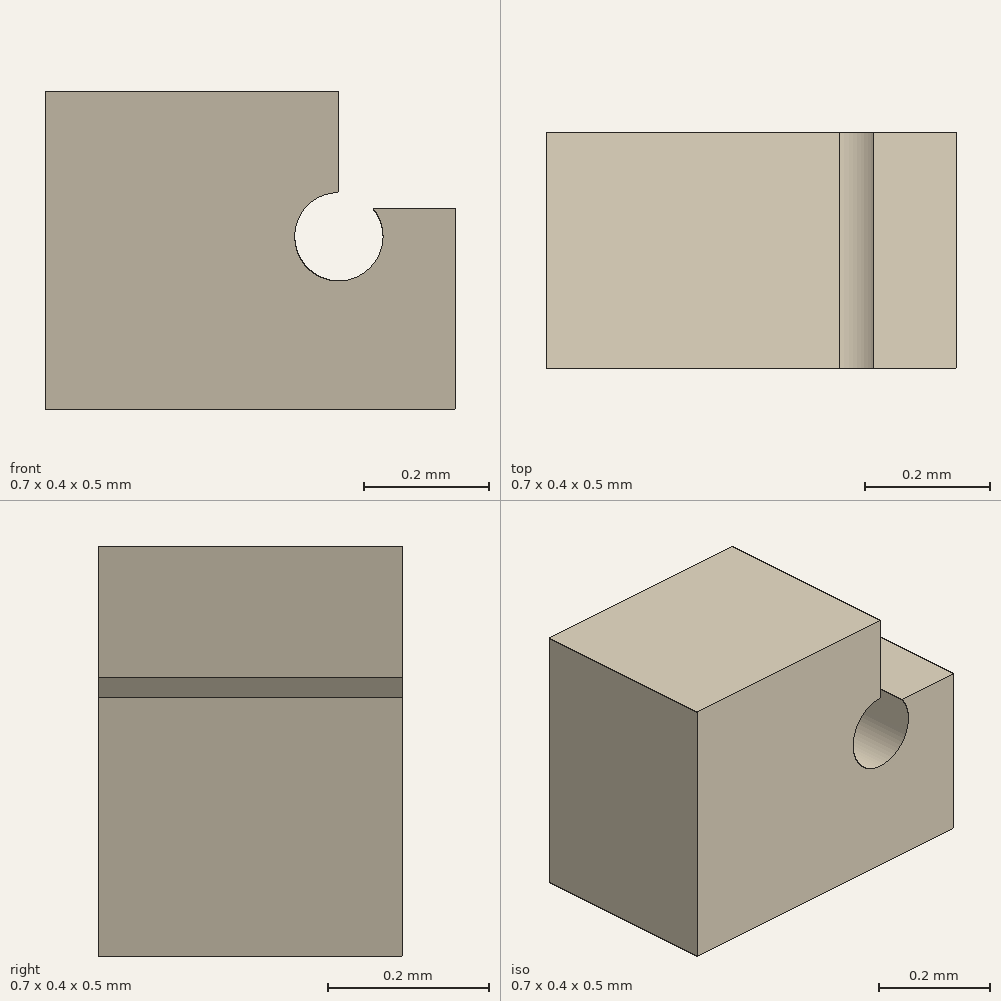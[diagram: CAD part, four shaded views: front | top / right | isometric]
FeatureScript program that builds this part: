
annotation { "Feature Type Name" : "Feature", "Feature Type Description" : "" }
export const myFeature = defineFeature(function(context is Context, id is Id, definition is map)
    precondition{}
    {
        {
            var Q0;
            Q0=qCreatedBy(makeId("Front.planeOp"),FACE);
            var sketch = newSketch(context, id + "F0", { "sketchPlane" : qUnion([Q0])});
            skLineSegment(sketch, "E0", {"start": v(0, 0) * mm, "end": v(0.94, 0) * mm});
            skLineSegment(sketch, "E1", {"start": v(0, 0) * mm, "end": v(0, 0.44) * mm});
            skLineSegment(sketch, "E2", {"start": v(0, 0.44) * mm, "end": v(0.94, 0.44) * mm});
            skLineSegment(sketch, "E3", {"start": v(0.94, 0.44) * mm, "end": v(0.94, 0) * mm});
            skLineSegment(sketch, "E4", {"start": v(0, 0.22) * mm, "end": v(0.94, 0.22) * mm});
            skLineSegment(sketch, "E5", {"start": v(0.47, 0.22) * mm, "end": v(0.47, 0.96) * mm});
            skLineSegment(sketch, "E6", {"start": v(0.47, 0.96) * mm, "end": v(0.66, 0.96) * mm});
            skLineSegment(sketch, "E7", {"start": v(0.47, 0.96) * mm, "end": v(0.28, 0.96) * mm});
            skLineSegment(sketch, "E8", {"start": v(0.66, 0.96) * mm, "end": v(0.66, 0.44) * mm});
            skLineSegment(sketch, "E9", {"start": v(0.28, 0.96) * mm, "end": v(0.28, 0.44) * mm});
            skCircle(sketch, "E10", {"center": v(0.47, 0.72) * mm, "radius": 0.07 * mm});
            skLineSegment(sketch, "E11", {"start": v(0.47, 0.72) * mm, "end": v(0.47, 0.22) * mm});
            skLineSegment(sketch, "E12", {"start": v(0.47, 0.72) * mm, "end": v(0.66, 0.72) * mm});
            skLineSegment(sketch, "E13", {"start": v(0.66, 0.72) * mm, "end": v(0.28, 0.72) * mm});
            skLineSegment(sketch, "E14.bottom", {"start": v(0.66, 0.96) * mm, "end": v(0.47, 0.96) * mm});
            skLineSegment(sketch, "E14.top", {"start": v(0.66, 0.77) * mm, "end": v(0.47, 0.77) * mm});
            skLineSegment(sketch, "E14.left", {"start": v(0.66, 0.96) * mm, "end": v(0.66, 0.77) * mm});
            skLineSegment(sketch, "E14.right", {"start": v(0.47, 0.96) * mm, "end": v(0.47, 0.77) * mm});
            skLineSegment(sketch, "E15", {"start": v(0.66, 0.77) * mm, "end": v(0.28, 0.77) * mm});
            skArc(sketch, "E16", {"start": v(0.66, 0.77) * mm, "mid": v(0.47, 0.96) * mm, "end": v(0.28, 0.77) * mm});
            skLineSegment(sketch, "E17.bottom", {"start": v(0.28, 0.96) * mm, "end": v(0, 0.96) * mm});
            skLineSegment(sketch, "E17.top", {"start": v(0.28, 0.44) * mm, "end": v(0, 0.44) * mm});
            skLineSegment(sketch, "E17.right", {"start": v(0, 0.96) * mm, "end": v(0, 0.44) * mm});
            skSolve(sketch);
        }
        {
            var Q0;
            {var subQ1=sQuery(id+"F0.wireOp",EDGE,"E15");var subQ3=sQuery(id+"F0.wireOp",EDGE,"E10");var subQ4=makeQuery(id+"F0.imprint","INTERSECT",VERTEX,{"disambiguationData":[OD(0.0)],"derivedFrom":[subQ3,subQ1]});Q0=makeQuery(id+"F0.imprint","IMPRINT",FACE,{"disambiguationData":[TD([[makeQuery(id+"F0.imprint","IMPRINT",EDGE,{"disambiguationData":[TD([[subQ4,-1.0]])],"derivedFrom":subQ3}),-1.0]])]});}
            var Q1;
            {var subQ1=sQuery(id+"F0.wireOp",EDGE,"E14.right");var subQ7=sQuery(id+"F0.wireOp",EDGE,"E10");var subQ9=makeQuery(id+"F0.imprint","INTERSECT",VERTEX,{"derivedFrom":[subQ7,subQ1]});Q1=makeQuery(id+"F0.imprint","IMPRINT",FACE,{"disambiguationData":[TD([[makeQuery(id+"F0.imprint","IMPRINT",EDGE,{"disambiguationData":[TD([[subQ9,-1.0]])],"derivedFrom":subQ7}),-1.0]])]});}
            var Q2;
            {var subQ0=sQuery(id+"F0.wireOp",EDGE,"E7");Q2=makeQuery(id+"F0.imprint","IMPRINT",FACE,{"disambiguationData":[TD([[makeQuery(id+"F0.imprint","IMPRINT",EDGE,{"derivedFrom":subQ0}),1.0]])]});}
            var Q3;
            {var subQ3=sQuery(id+"F0.wireOp",EDGE,"E17.bottom");Q3=makeQuery(id+"F0.imprint","IMPRINT",FACE,{"disambiguationData":[TD([[makeQuery(id+"F0.imprint","IMPRINT",EDGE,{"derivedFrom":subQ3}),1.0]])]});}
            var Q4;
            {var subQ1=sQuery(id+"F0.wireOp",EDGE,"E13");var subQ3=sQuery(id+"F0.wireOp",EDGE,"E10");var subQ4=makeQuery(id+"F0.imprint","INTERSECT",VERTEX,{"disambiguationData":[OD(1.0)],"derivedFrom":[subQ3,subQ1]});Q4=makeQuery(id+"F0.imprint","IMPRINT",FACE,{"disambiguationData":[TD([[makeQuery(id+"F0.imprint","IMPRINT",EDGE,{"disambiguationData":[TD([[subQ4,-1.0]])],"derivedFrom":subQ3}),-1.0]])]});}
            var Q5;
            {var subQ0=sQuery(id+"F0.wireOp",EDGE,"E15");var subQ1=sQuery(id+"F0.wireOp",EDGE,"E10");var subQ2=makeQuery(id+"F0.imprint","INTERSECT",VERTEX,{"disambiguationData":[OD(1.0)],"derivedFrom":[subQ1,subQ0]});Q5=makeQuery(id+"F0.imprint","IMPRINT",FACE,{"disambiguationData":[TD([[makeQuery(id+"F0.imprint","IMPRINT",EDGE,{"disambiguationData":[TD([[subQ2,-1.0]])],"derivedFrom":subQ1}),-1.0]])]});}
            var Q6;
            {var subQ0=sQuery(id+"F0.wireOp",EDGE,"E15");var subQ5=sQuery(id+"F0.wireOp",EDGE,"E10");var subQ6=makeQuery(id+"F0.imprint","INTERSECT",VERTEX,{"disambiguationData":[OD(0.0)],"derivedFrom":[subQ5,subQ0]});Q6=makeQuery(id+"F0.imprint","IMPRINT",FACE,{"disambiguationData":[TD([[makeQuery(id+"F0.imprint","IMPRINT",EDGE,{"disambiguationData":[TD([[subQ6,1.0]])],"derivedFrom":subQ5}),-1.0]])]});}
            var Q7;
            {var subQ1=sQuery(id+"F0.wireOp",EDGE,"E2");var subQ5=sQuery(id+"F0.wireOp",EDGE,"E8");var subQ6=makeQuery(id+"F0.imprint","INTERSECT",VERTEX,{"derivedFrom":[subQ1,subQ5]});Q7=makeQuery(id+"F0.imprint","IMPRINT",FACE,{"disambiguationData":[TD([[makeQuery(id+"F0.imprint","IMPRINT",EDGE,{"disambiguationData":[TD([[subQ6,1.0]])],"derivedFrom":subQ1}),1.0]])]});}
            extrude(context, id + "F1", {"entities" : qUnion([Q0, Q1, Q2, Q3, Q4, Q5, Q6, Q7]), "depth" : .38 * mm});
        }
    });
